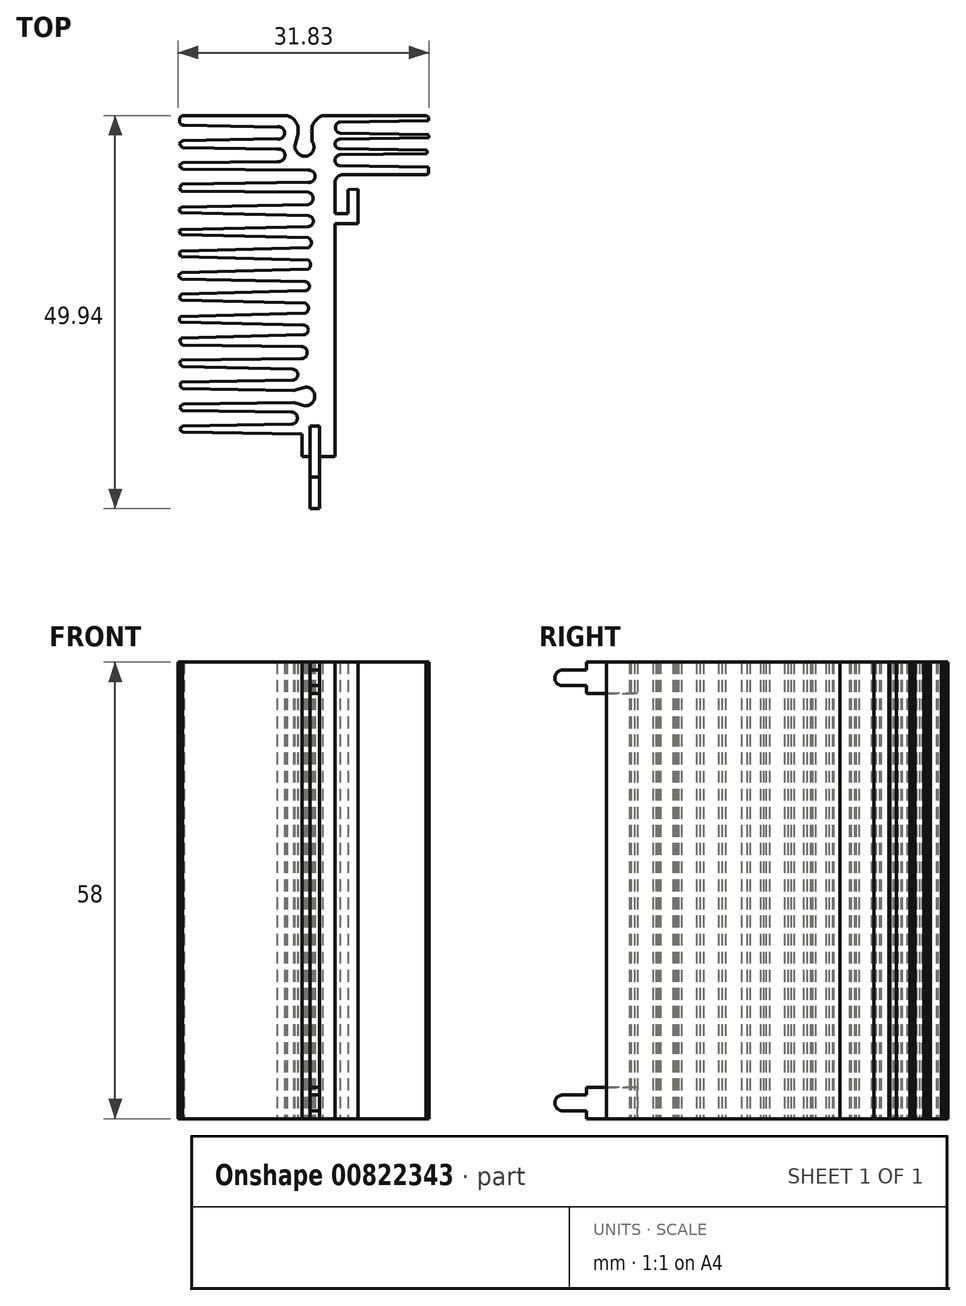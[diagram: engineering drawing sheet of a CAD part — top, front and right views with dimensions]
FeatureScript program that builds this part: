
annotation { "Feature Type Name" : "Feature", "Feature Type Description" : "" }
export const myFeature = defineFeature(function(context is Context, id is Id, definition is map)
    precondition{}
    {
        {
            var Q0;
            Q0=qCreatedBy(makeId("Top.planeOp"),FACE);
            var sketch = newSketch(context, id + "F0", { "sketchPlane" : qUnion([Q0])});
            skLineSegment(sketch, "E0", {"start": v(-17.11, 24.3) * mm, "end": v(-4.07, 24.3) * mm});
            skArc(sketch, "E1", {"start": v(-17.11, 24.3) * mm, "mid": v(-17.73, 23.67) * mm, "end": v(-17.11, 23.05) * mm});
            skLineSegment(sketch, "E2", {"start": v(-17.11, 23.05) * mm, "end": v(-5.31, 22.84) * mm});
            skArc(sketch, "E3", {"start": v(-5.31, 21.33) * mm, "mid": v(-4.36, 22.09) * mm, "end": v(-5.31, 22.84) * mm});
            skLineSegment(sketch, "E4", {"start": v(-5.31, 21.33) * mm, "end": v(-17.33, 21.08) * mm});
            skLineSegment(sketch, "E5", {"start": v(-17.33, 21.08) * mm, "end": v(-17.75, 20.7) * mm});
            skLineSegment(sketch, "E6", {"start": v(-17.75, 20.7) * mm, "end": v(-17.33, 20.24) * mm});
            skLineSegment(sketch, "E7", {"start": v(-17.33, 20.24) * mm, "end": v(-5.31, 20.02) * mm});
            skArc(sketch, "E8", {"start": v(-5.31, 18.47) * mm, "mid": v(-4.32, 19.24) * mm, "end": v(-5.31, 20.02) * mm});
            skLineSegment(sketch, "E9", {"start": v(-5.31, 18.47) * mm, "end": v(-17.34, 18.31) * mm});
            skLineSegment(sketch, "E10", {"start": v(-17.34, 18.31) * mm, "end": v(-17.75, 17.94) * mm});
            skLineSegment(sketch, "E11", {"start": v(-17.75, 17.94) * mm, "end": v(-17.34, 17.48) * mm});
            skLineSegment(sketch, "E12", {"start": v(-17.34, 17.48) * mm, "end": v(-1.39, 17.34) * mm});
            skArc(sketch, "E13", {"start": v(-1.39, 15.8) * mm, "mid": v(-0.5, 16.57) * mm, "end": v(-1.39, 17.34) * mm});
            skLineSegment(sketch, "E14", {"start": v(-1.39, 15.8) * mm, "end": v(-17.35, 15.6) * mm});
            skLineSegment(sketch, "E15", {"start": v(-17.35, 15.6) * mm, "end": v(-17.74, 15.14) * mm});
            skLineSegment(sketch, "E16", {"start": v(-17.74, 15.14) * mm, "end": v(-17.5, 14.71) * mm});
            skLineSegment(sketch, "E17", {"start": v(-17.5, 14.71) * mm, "end": v(-1.39, 14.57) * mm});
            skArc(sketch, "E18", {"start": v(-1.39, 12.97) * mm, "mid": v(-0.74, 13.77) * mm, "end": v(-1.39, 14.57) * mm});
            skLineSegment(sketch, "E19", {"start": v(-1.39, 12.97) * mm, "end": v(-17.43, 12.63) * mm});
            skLineSegment(sketch, "E20", {"start": v(-17.43, 12.63) * mm, "end": v(-17.74, 12.4) * mm});
            skLineSegment(sketch, "E21", {"start": v(-17.74, 12.4) * mm, "end": v(-17.56, 11.96) * mm});
            skLineSegment(sketch, "E22", {"start": v(-17.56, 11.96) * mm, "end": v(-1.39, 11.56) * mm});
            skArc(sketch, "E23", {"start": v(-1.39, 10.18) * mm, "mid": v(-0.71, 10.87) * mm, "end": v(-1.39, 11.56) * mm});
            skLineSegment(sketch, "E24", {"start": v(-1.39, 10.18) * mm, "end": v(-17.43, 9.78) * mm});
            skLineSegment(sketch, "E25", {"start": v(-17.43, 9.78) * mm, "end": v(-17.57, 9.78) * mm});
            skLineSegment(sketch, "E26", {"start": v(-17.57, 9.78) * mm, "end": v(-17.74, 9.6) * mm});
            skLineSegment(sketch, "E27", {"start": v(-17.74, 9.6) * mm, "end": v(-17.53, 9.19) * mm});
            skLineSegment(sketch, "E28", {"start": v(-17.53, 9.19) * mm, "end": v(-1.39, 8.79) * mm});
            skArc(sketch, "E29", {"start": v(-1.39, 7.5) * mm, "mid": v(-0.96, 8.14) * mm, "end": v(-1.39, 8.79) * mm});
            skLineSegment(sketch, "E30", {"start": v(-1.39, 7.5) * mm, "end": v(-17.53, 7.07) * mm});
            skLineSegment(sketch, "E31", {"start": v(-17.53, 7.07) * mm, "end": v(-17.76, 6.84) * mm});
            skLineSegment(sketch, "E32", {"start": v(-17.76, 6.84) * mm, "end": v(-17.53, 6.36) * mm});
            skLineSegment(sketch, "E33", {"start": v(-17.53, 6.36) * mm, "end": v(-1.39, 5.96) * mm});
            skArc(sketch, "E34", {"start": v(-1.39, 4.76) * mm, "mid": v(-1.06, 5.36) * mm, "end": v(-1.39, 5.96) * mm});
            skLineSegment(sketch, "E35", {"start": v(-1.39, 4.76) * mm, "end": v(-17.47, 4.34) * mm});
            skLineSegment(sketch, "E36", {"start": v(-17.47, 4.34) * mm, "end": v(-17.87, 3.98) * mm});
            skLineSegment(sketch, "E37", {"start": v(-17.87, 3.98) * mm, "end": v(-17.47, 3.54) * mm});
            skLineSegment(sketch, "E38", {"start": v(-17.47, 3.54) * mm, "end": v(-1.77, 3.19) * mm});
            skArc(sketch, "E39", {"start": v(-1.77, 2.03) * mm, "mid": v(-1.2, 2.6) * mm, "end": v(-1.77, 3.19) * mm});
            skLineSegment(sketch, "E40", {"start": v(-1.77, 2.03) * mm, "end": v(-17.47, 1.62) * mm});
            skLineSegment(sketch, "E41", {"start": v(-17.47, 1.62) * mm, "end": v(-17.75, 1.2) * mm});
            skLineSegment(sketch, "E42", {"start": v(-17.75, 1.2) * mm, "end": v(-17.47, 0.88) * mm});
            skLineSegment(sketch, "E43", {"start": v(-17.47, 0.88) * mm, "end": v(-1.77, 0.48) * mm});
            skArc(sketch, "E44", {"start": v(-1.77, -0.83) * mm, "mid": v(-1.33, -0.18) * mm, "end": v(-1.77, 0.48) * mm});
            skLineSegment(sketch, "E45", {"start": v(-1.77, -0.83) * mm, "end": v(-17.55, -1.24) * mm});
            skArc(sketch, "E46", {"start": v(-17.55, -1.24) * mm, "mid": v(-17.71, -1.6) * mm, "end": v(-17.55, -1.96) * mm});
            skLineSegment(sketch, "E47", {"start": v(-17.55, -1.96) * mm, "end": v(-1.96, -2.31) * mm});
            skArc(sketch, "E48", {"start": v(-1.96, -3.56) * mm, "mid": v(-1.35, -2.94) * mm, "end": v(-1.96, -2.31) * mm});
            skLineSegment(sketch, "E49", {"start": v(-1.96, -3.56) * mm, "end": v(-17.51, -3.96) * mm});
            skLineSegment(sketch, "E50", {"start": v(-17.51, -3.96) * mm, "end": v(-17.73, -4.4) * mm});
            skLineSegment(sketch, "E51", {"start": v(-17.73, -4.4) * mm, "end": v(-17.31, -4.86) * mm});
            skLineSegment(sketch, "E52", {"start": v(-17.31, -4.86) * mm, "end": v(-2.26, -5.04) * mm});
            skArc(sketch, "E53", {"start": v(-2.26, -6.6) * mm, "mid": v(-1.49, -5.82) * mm, "end": v(-2.26, -5.04) * mm});
            skLineSegment(sketch, "E54", {"start": v(-2.26, -6.6) * mm, "end": v(-17.53, -6.78) * mm});
            skLineSegment(sketch, "E55", {"start": v(-17.53, -6.78) * mm, "end": v(-17.73, -7.2) * mm});
            skLineSegment(sketch, "E56", {"start": v(-17.73, -7.2) * mm, "end": v(-17.35, -7.62) * mm});
            skLineSegment(sketch, "E57", {"start": v(-17.35, -7.62) * mm, "end": v(-3.36, -7.94) * mm});
            skArc(sketch, "E58", {"start": v(-3.36, -9.33) * mm, "mid": v(-2.68, -8.63) * mm, "end": v(-3.36, -7.94) * mm});
            skLineSegment(sketch, "E59", {"start": v(-3.36, -9.33) * mm, "end": v(-17.47, -9.55) * mm});
            skLineSegment(sketch, "E60", {"start": v(-17.47, -9.55) * mm, "end": v(-17.71, -9.92) * mm});
            skLineSegment(sketch, "E61", {"start": v(-17.71, -9.92) * mm, "end": v(-17.34, -10.42) * mm});
            skLineSegment(sketch, "E62", {"start": v(-17.34, -10.42) * mm, "end": v(-3.23, -10.61) * mm});
            skLineSegment(sketch, "E63", {"start": v(-3.23, -10.61) * mm, "end": v(-1.7, -10.18) * mm});
            skArc(sketch, "E64", {"start": v(-1.7, -12.59) * mm, "mid": v(-0.53, -11.38) * mm, "end": v(-1.7, -10.18) * mm});
            skLineSegment(sketch, "E65", {"start": v(-1.7, -12.59) * mm, "end": v(-3.19, -12.2) * mm});
            skLineSegment(sketch, "E66", {"start": v(-3.19, -12.2) * mm, "end": v(-17.28, -12.35) * mm});
            skLineSegment(sketch, "E67", {"start": v(-17.28, -12.35) * mm, "end": v(-17.73, -12.76) * mm});
            skLineSegment(sketch, "E68", {"start": v(-17.73, -12.76) * mm, "end": v(-17.36, -13.17) * mm});
            skLineSegment(sketch, "E69", {"start": v(-17.36, -13.17) * mm, "end": v(-3.51, -13.36) * mm});
            skArc(sketch, "E70", {"start": v(-3.51, -14.93) * mm, "mid": v(-2.74, -14.15) * mm, "end": v(-3.51, -13.36) * mm});
            skLineSegment(sketch, "E71", {"start": v(-3.51, -14.93) * mm, "end": v(-17.35, -15.14) * mm});
            skLineSegment(sketch, "E72", {"start": v(-17.35, -15.14) * mm, "end": v(-17.7, -15.53) * mm});
            skLineSegment(sketch, "E73", {"start": v(-17.7, -15.53) * mm, "end": v(-17.35, -15.94) * mm});
            skLineSegment(sketch, "E74", {"start": v(-17.35, -15.94) * mm, "end": v(-2.17, -16.15) * mm});
            skLineSegment(sketch, "E75", {"start": v(-2.17, -16.15) * mm, "end": v(-2.17, -19.03) * mm});
            skLineSegment(sketch, "E76", {"start": v(-2.17, -19.03) * mm, "end": v(-1.12, -19.03) * mm});
            skLineSegment(sketch, "E77", {"start": v(-1.12, -19.03) * mm, "end": v(-1.12, -15.14) * mm});
            skLineSegment(sketch, "E78", {"start": v(-1.12, -15.14) * mm, "end": v(0.05, -15.14) * mm});
            skLineSegment(sketch, "E79", {"start": v(0.05, -15.14) * mm, "end": v(0.05, -25.64) * mm});
            skLineSegment(sketch, "E80", {"start": v(0.05, -25.64) * mm, "end": v(-1.12, -25.64) * mm});
            skLineSegment(sketch, "E81", {"start": v(-1.12, -25.64) * mm, "end": v(-1.12, -19.03) * mm});
            skLineSegment(sketch, "E82", {"start": v(0.05, -21.63) * mm, "end": v(-1.12, -21.63) * mm});
            skLineSegment(sketch, "E83", {"start": v(0.05, -24.68) * mm, "end": v(-1.12, -24.68) * mm});
            skLineSegment(sketch, "E84", {"start": v(0.05, -19.05) * mm, "end": v(2.04, -19.05) * mm});
            skLineSegment(sketch, "E85", {"start": v(2.04, -19.05) * mm, "end": v(2.04, 10.55) * mm});
            skLineSegment(sketch, "E86", {"start": v(2.04, 10.55) * mm, "end": v(4.96, 10.55) * mm});
            skLineSegment(sketch, "E87", {"start": v(4.96, 10.55) * mm, "end": v(4.96, 14.92) * mm});
            skLineSegment(sketch, "E88", {"start": v(4.96, 14.92) * mm, "end": v(3.7, 14.9) * mm});
            skLineSegment(sketch, "E89", {"start": v(3.7, 14.9) * mm, "end": v(3.7, 11.81) * mm});
            skLineSegment(sketch, "E90", {"start": v(3.7, 11.81) * mm, "end": v(2.04, 11.81) * mm});
            skLineSegment(sketch, "E91", {"start": v(2.04, 11.81) * mm, "end": v(2.04, 15.77) * mm});
            skArc(sketch, "E92", {"start": v(3.06, 16.78) * mm, "mid": v(2.34, 16.48) * mm, "end": v(2.04, 15.77) * mm});
            skLineSegment(sketch, "E93", {"start": v(3.06, 16.78) * mm, "end": v(13.63, 16.78) * mm});
            skLineSegment(sketch, "E94", {"start": v(13.63, 16.78) * mm, "end": v(13.91, 16.93) * mm});
            skLineSegment(sketch, "E95", {"start": v(13.91, 16.93) * mm, "end": v(13.91, 17.74) * mm});
            skLineSegment(sketch, "E96", {"start": v(13.91, 17.74) * mm, "end": v(2.7, 17.91) * mm});
            skArc(sketch, "E97", {"start": v(2.7, 19.3) * mm, "mid": v(2.03, 18.6) * mm, "end": v(2.7, 17.91) * mm});
            skLineSegment(sketch, "E98", {"start": v(2.7, 19.3) * mm, "end": v(13.7, 19.47) * mm});
            skLineSegment(sketch, "E99", {"start": v(13.7, 19.47) * mm, "end": v(13.7, 19.9) * mm});
            skLineSegment(sketch, "E100", {"start": v(13.7, 19.9) * mm, "end": v(2.7, 20.09) * mm});
            skArc(sketch, "E101", {"start": v(2.7, 21.27) * mm, "mid": v(2.04, 20.68) * mm, "end": v(2.7, 20.09) * mm});
            skLineSegment(sketch, "E102", {"start": v(2.7, 21.27) * mm, "end": v(13.96, 21.47) * mm});
            skLineSegment(sketch, "E103", {"start": v(13.96, 21.47) * mm, "end": v(13.95, 21.87) * mm});
            skLineSegment(sketch, "E104", {"start": v(13.95, 21.87) * mm, "end": v(2.7, 22.06) * mm});
            skArc(sketch, "E105", {"start": v(2.7, 23.47) * mm, "mid": v(2.08, 22.77) * mm, "end": v(2.7, 22.06) * mm});
            skLineSegment(sketch, "E106", {"start": v(2.7, 23.47) * mm, "end": v(13.9, 23.66) * mm});
            skLineSegment(sketch, "E107", {"start": v(13.9, 23.66) * mm, "end": v(13.9, 24.09) * mm});
            skLineSegment(sketch, "E108", {"start": v(13.9, 24.09) * mm, "end": v(13.7, 24.27) * mm});
            skLineSegment(sketch, "E109", {"start": v(13.7, 24.27) * mm, "end": v(0.46, 24.27) * mm});
            skArc(sketch, "E110", {"start": v(0.46, 24.27) * mm, "mid": v(-0.65, 23.37) * mm, "end": v(-0.86, 21.95) * mm});
            skLineSegment(sketch, "E111", {"start": v(-0.86, 21.95) * mm, "end": v(-0.86, 21.02) * mm});
            skArc(sketch, "E112", {"start": v(-1.9, 19.12) * mm, "mid": v(-0.77, 19.73) * mm, "end": v(-0.86, 21.02) * mm});
            skArc(sketch, "E113", {"start": v(-3.07, 20.29) * mm, "mid": v(-2.67, 19.51) * mm, "end": v(-1.9, 19.12) * mm});
            skLineSegment(sketch, "E114", {"start": v(-3.07, 20.29) * mm, "end": v(-2.68, 21.9) * mm});
            skArc(sketch, "E115", {"start": v(-2.68, 21.9) * mm, "mid": v(-2.9, 23.38) * mm, "end": v(-4.07, 24.3) * mm});
            skSolve(sketch);
        }
        {
            var Q0;
            Q0=makeQuery(id+"F0.imprint","IMPRINT",FACE,{"disambiguationData":[TD([[makeQuery(id+"F0.imprint","IMPRINT",EDGE,{"derivedFrom":sQuery(id+"F0.wireOp",EDGE,"E0")}),-1.0]])]});
            extrude(context, id + "F1", {"entities" : qUnion([Q0]), "endBound" : BoundingType.SYMMETRIC, "depth" : 58 * mm, "offsetDistance" : 25 * mm});
        }
        {
            var Q0;
            {var subQ4=sQuery(id+"F0.wireOp",EDGE,"E77");Q0=makeQuery(id+"F0.imprint","IMPRINT",FACE,{"disambiguationData":[TD([[makeQuery(id+"F0.imprint","IMPRINT",EDGE,{"derivedFrom":subQ4}),-1.0]])]});}
            extrude(context, id + "F2", {"entities" : qUnion([Q0]), "depth" : 29 * mm, "offsetDistance" : 25 * mm, "hasSecondDirection" : true, "secondDirectionOppositeDirection" : false, "secondDirectionDepth" : 25 * mm});
        }
        {
            var Q0;
            {var subQ4=sQuery(id+"F0.wireOp",EDGE,"E77");Q0=makeQuery(id+"F0.imprint","IMPRINT",FACE,{"disambiguationData":[TD([[makeQuery(id+"F0.imprint","IMPRINT",EDGE,{"derivedFrom":subQ4}),-1.0]])]});}
            extrude(context, id + "F3", {"entities" : qUnion([Q0]), "oppositeDirection" : true, "depth" : 29 * mm, "offsetDistance" : 25 * mm, "hasSecondDirection" : true, "secondDirectionOppositeDirection" : true, "secondDirectionDepth" : 25 * mm});
        }
        {
            var Q0;
            {var subQ0=sQuery(id+"F0.wireOp",EDGE,"E82");Q0=makeQuery(id+"F0.imprint","IMPRINT",FACE,{"disambiguationData":[TD([[makeQuery(id+"F0.imprint","IMPRINT",EDGE,{"derivedFrom":subQ0}),1.0]])]});}
            var Q1;
            {var subQ0=sQuery(id+"F0.wireOp",EDGE,"E80");Q1=makeQuery(id+"F0.imprint","IMPRINT",FACE,{"disambiguationData":[TD([[makeQuery(id+"F0.imprint","IMPRINT",EDGE,{"derivedFrom":subQ0}),-1.0]])]});}
            extrude(context, id + "F4", {"entities" : qUnion([Q0, Q1]), "operationType" : NewBodyOperationType.ADD, "depth" : 28 * mm, "offsetDistance" : 25 * mm, "hasSecondDirection" : true, "secondDirectionOppositeDirection" : false, "secondDirectionDepth" : 26 * mm});
        }
        {
            var Q0;
            {var subQ0=sQuery(id+"F0.wireOp",EDGE,"E82");Q0=makeQuery(id+"F0.imprint","IMPRINT",FACE,{"disambiguationData":[TD([[makeQuery(id+"F0.imprint","IMPRINT",EDGE,{"derivedFrom":subQ0}),1.0]])]});}
            var Q1;
            {var subQ0=sQuery(id+"F0.wireOp",EDGE,"E80");Q1=makeQuery(id+"F0.imprint","IMPRINT",FACE,{"disambiguationData":[TD([[makeQuery(id+"F0.imprint","IMPRINT",EDGE,{"derivedFrom":subQ0}),-1.0]])]});}
            extrude(context, id + "F5", {"entities" : qUnion([Q0, Q1]), "operationType" : NewBodyOperationType.ADD, "oppositeDirection" : true, "depth" : 28 * mm, "offsetDistance" : 25 * mm, "hasSecondDirection" : true, "secondDirectionOppositeDirection" : true, "secondDirectionDepth" : 26 * mm});
        }
        {
            var Q0;
            Q0=makeQuery(id+"F4.opExtrude","CAP_EDGE",EDGE,{"disambiguationData":[OSD([sQuery(id+"F0.wireOp",EDGE,"E80")])],"isStart":false});
            var Q1;
            Q1=makeQuery(id+"F4.opExtrude","CAP_EDGE",EDGE,{"disambiguationData":[OSD([sQuery(id+"F0.wireOp",EDGE,"E80")])],"isStart":true});
            var Q2;
            Q2=makeQuery(id+"F5.opExtrude","CAP_EDGE",EDGE,{"disambiguationData":[OSD([sQuery(id+"F0.wireOp",EDGE,"E80")])],"isStart":true});
            var Q3;
            Q3=makeQuery(id+"F5.opExtrude","CAP_EDGE",EDGE,{"disambiguationData":[OSD([sQuery(id+"F0.wireOp",EDGE,"E80")])],"isStart":false});
            fillet(context, id + "F6", {"entities" : qUnion([Q0, Q1, Q2, Q3]), "radius" : 1 * mm, "tangentPropagation" : true, "allowEdgeOverflow" : false});
        }
    });
